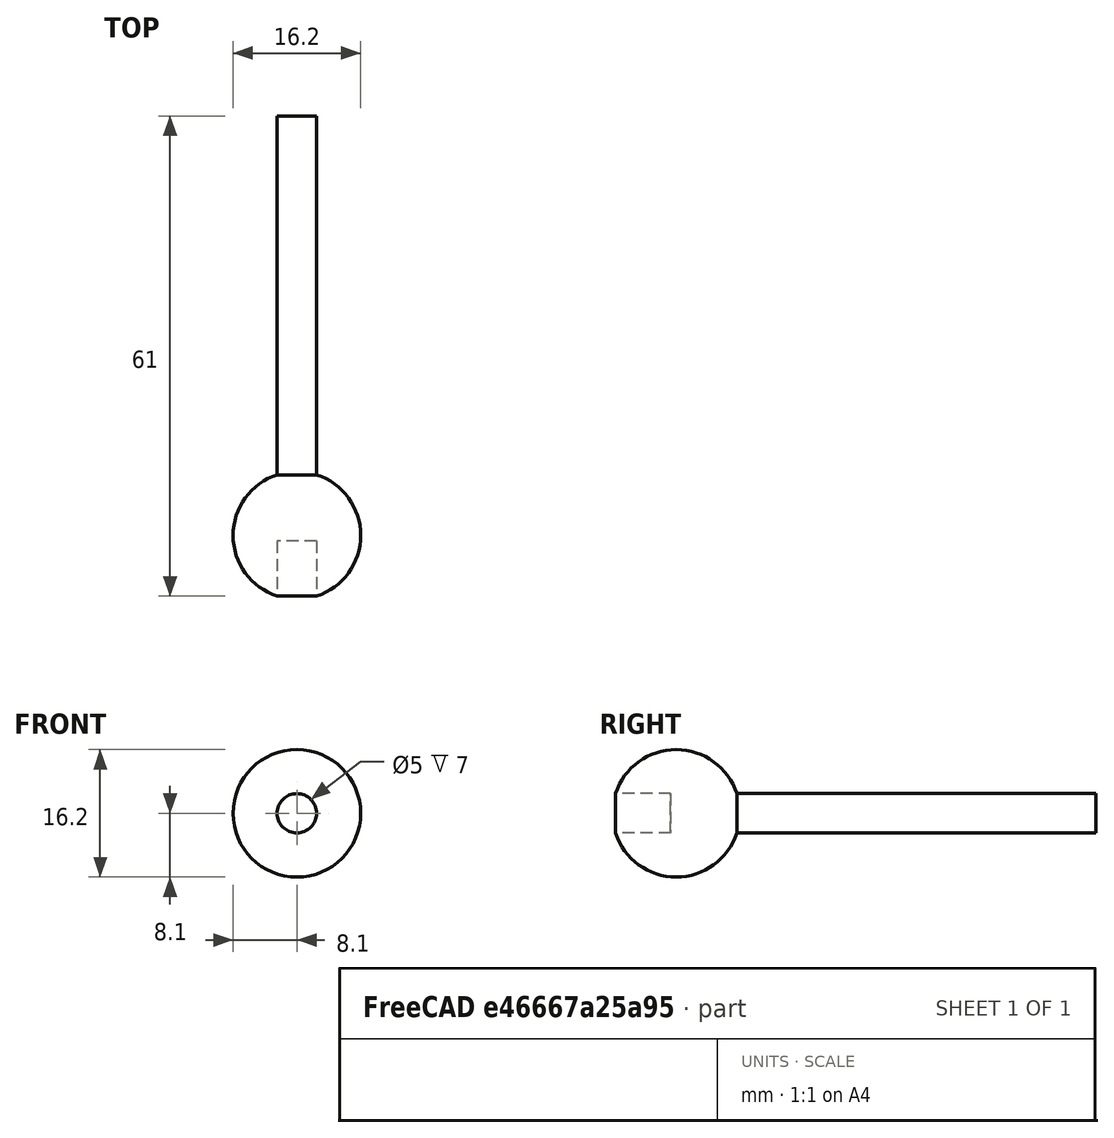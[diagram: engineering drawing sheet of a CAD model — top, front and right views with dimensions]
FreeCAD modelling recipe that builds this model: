
FCSTD DOCUMENT  (FreeCAD 0.16R6706 (Git))
Label: 3d_Kugelstab
License: All rights reserved
LicenseURL: http://de.wikipedia.org/wiki/Alle_Rechte_vorbehalten
objects: Sketcher::SketchObject×1, PartDesign::Revolution×1
note: 3 computed .brp shape members not serialized (recipe doc carries the construction recipe); baked Part::Feature solids carry a one-line shape summary decoded from their .brp

FEATURE [Sketcher::SketchObject] Sketch
  sketch-geometry (6):
    g0: ArcOfCircle CenterX=0 CenterY=8.1 CenterZ=0 NormalX=0 NormalY=0 NormalZ=1 Radius=8.1 StartAngle=5.02615 EndAngle=7.54022
    g1: LineSegment StartX=2.5 StartY=7.395 StartZ=0 EndX=2.5 EndY=0.395456 EndZ=0
    g2: LineSegment StartX=0 StartY=7.395 StartZ=0 EndX=2.5 EndY=7.395 EndZ=0
    g3: LineSegment StartX=2.5 StartY=61.395 StartZ=0 EndX=2.5 EndY=15.8045 EndZ=0
    g4: LineSegment StartX=0 StartY=61.395 StartZ=0 EndX=2.5 EndY=61.395 EndZ=0
    g5: LineSegment StartX=0 StartY=61.395 StartZ=0 EndX=0 EndY=7.395 EndZ=0
  constraints (19):
    c: DistanceX(g-1,g0) = 0
    c: Vertical(g1)
    c: Horizontal(g2)
    c: DistanceX(g2,g2) = 2.5
    c: Coincident(g2,g1)
    c: Vertical(g3)
    c: DistanceY(g-1,g3) = 61.395
    c: DistanceX(g-1,g3) = 2.5
    c: Horizontal(g4)
    c: DistanceX(g4,g4) = 2.5
    c: Coincident(g4,g3)
    c: Vertical(g5)
    c: DistanceY(g5,g5) = 54
    c: Coincident(g5,g4)
    c: Coincident(g1,g0)
    c: DistanceY(g-1,g0) = 8.1
    c: Coincident(g0,g3)
    c: Coincident(g2,g5)
    c: Distance(g0,g0) = 8.1
FEATURE [PartDesign::Revolution] Revolution
  Angle = 360
  Axis = (0,1,0)
  Base = (0,0,0)
  ReferenceAxis = -> Sketch [V_Axis]
  Reversed = true
  Sketch = -> Sketch
